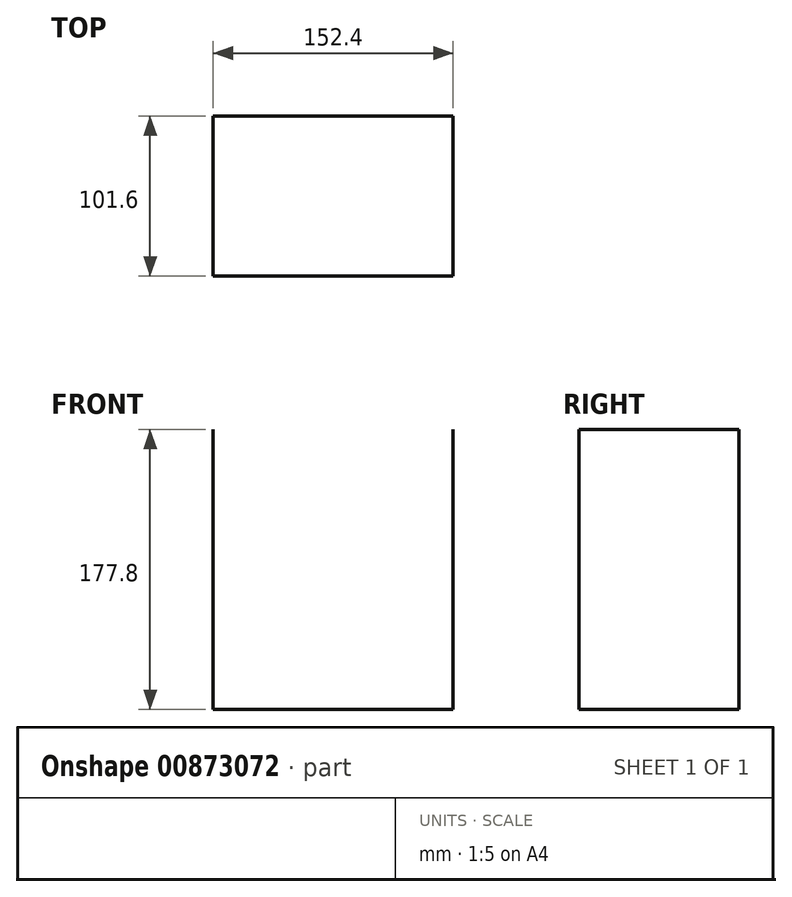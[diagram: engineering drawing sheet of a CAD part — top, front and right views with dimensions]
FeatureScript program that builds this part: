
annotation { "Feature Type Name" : "Feature", "Feature Type Description" : "" }
export const myFeature = defineFeature(function(context is Context, id is Id, definition is map)
    precondition{}
    {
        {
            var Q0;
            Q0=qCreatedBy(makeId("Front.planeOp"),FACE);
            var sketch = newSketch(context, id + "F0", { "sketchPlane" : qUnion([Q0])});
            skLineSegment(sketch, "E0", {"start": v(-76.62, -89.28) * mm, "end": v(75.78, -89.28) * mm});
            skLineSegment(sketch, "E1", {"start": v(-76.62, -89.28) * mm, "end": v(-76.62, 88.52) * mm});
            skLineSegment(sketch, "E2", {"start": v(75.78, -89.28) * mm, "end": v(75.78, 88.52) * mm});
            skLineSegment(sketch, "E3", {"start": v(-76.62, 88.52) * mm, "end": v(75.78, 88.52) * mm});
            skSolve(sketch);
        }
        {
            var Q0;
            Q0=makeQuery(id+"F0.imprint","IMPRINT",FACE,{"disambiguationData":[TD([[makeQuery(id+"F0.imprint","IMPRINT",EDGE,{"derivedFrom":sQuery(id+"F0.wireOp",EDGE,"E0")}),1.0]])]});
            var sketch = newSketch(context, id + "F1", { "sketchPlane" : qUnion([Q0])});
            skLineSegment(sketch, "E4", {"start": v(-76.29, -63.5) * mm, "end": v(76.11, -63.5) * mm});
            skLineSegment(sketch, "E5", {"start": v(-76.29, -38.1) * mm, "end": v(76.11, -38.1) * mm});
            skLineSegment(sketch, "E6", {"start": v(-76.29, -12.7) * mm, "end": v(76.11, -12.7) * mm});
            skLineSegment(sketch, "E7", {"start": v(-76.29, 0) * mm, "end": v(76.11, 0) * mm});
            skLineSegment(sketch, "E8", {"start": v(-76.29, 12.7) * mm, "end": v(76.11, 12.7) * mm});
            skLineSegment(sketch, "E9", {"start": v(-76.46, 25.4) * mm, "end": v(75.94, 25.4) * mm});
            skLineSegment(sketch, "E10", {"start": v(-76.11, 38.1) * mm, "end": v(76.29, 38.1) * mm});
            skLineSegment(sketch, "E11", {"start": v(-76.11, 50.8) * mm, "end": v(76.29, 50.8) * mm});
            skLineSegment(sketch, "E12", {"start": v(-76.12, 63.5) * mm, "end": v(76.28, 63.5) * mm});
            skLineSegment(sketch, "E13", {"start": v(-76.29, -50.8) * mm, "end": v(76.11, -50.8) * mm});
            skLineSegment(sketch, "E14", {"start": v(-76.29, -25.4) * mm, "end": v(76.11, -25.4) * mm});
            skLineSegment(sketch, "E15", {"start": v(-76.44, -76.2) * mm, "end": v(75.96, -76.2) * mm});
            skSolve(sketch);
        }
        {
            var Q0;
            Q0=sQuery(id+"F0.wireOp",EDGE,"E1");
            extrude(context, id + "F2", {"bodyType" : ToolBodyType.SURFACE, "surfaceEntities" : qUnion([Q0]), "depth" : 101.6 * mm, "offsetDistance" : 25.4 * mm});
        }
        {
            var Q0;
            Q0=sQuery(id+"F0.wireOp",EDGE,"E2");
            extrude(context, id + "F3", {"bodyType" : ToolBodyType.SURFACE, "surfaceEntities" : qUnion([Q0]), "depth" : 101.6 * mm, "offsetDistance" : 25.4 * mm});
        }
        {
            var Q0;
            Q0=sQuery(id+"F0.wireOp",EDGE,"E0");
            extrude(context, id + "F4", {"bodyType" : ToolBodyType.SURFACE, "surfaceEntities" : qUnion([Q0]), "depth" : 101.6 * mm, "offsetDistance" : 25.4 * mm});
        }
    });
